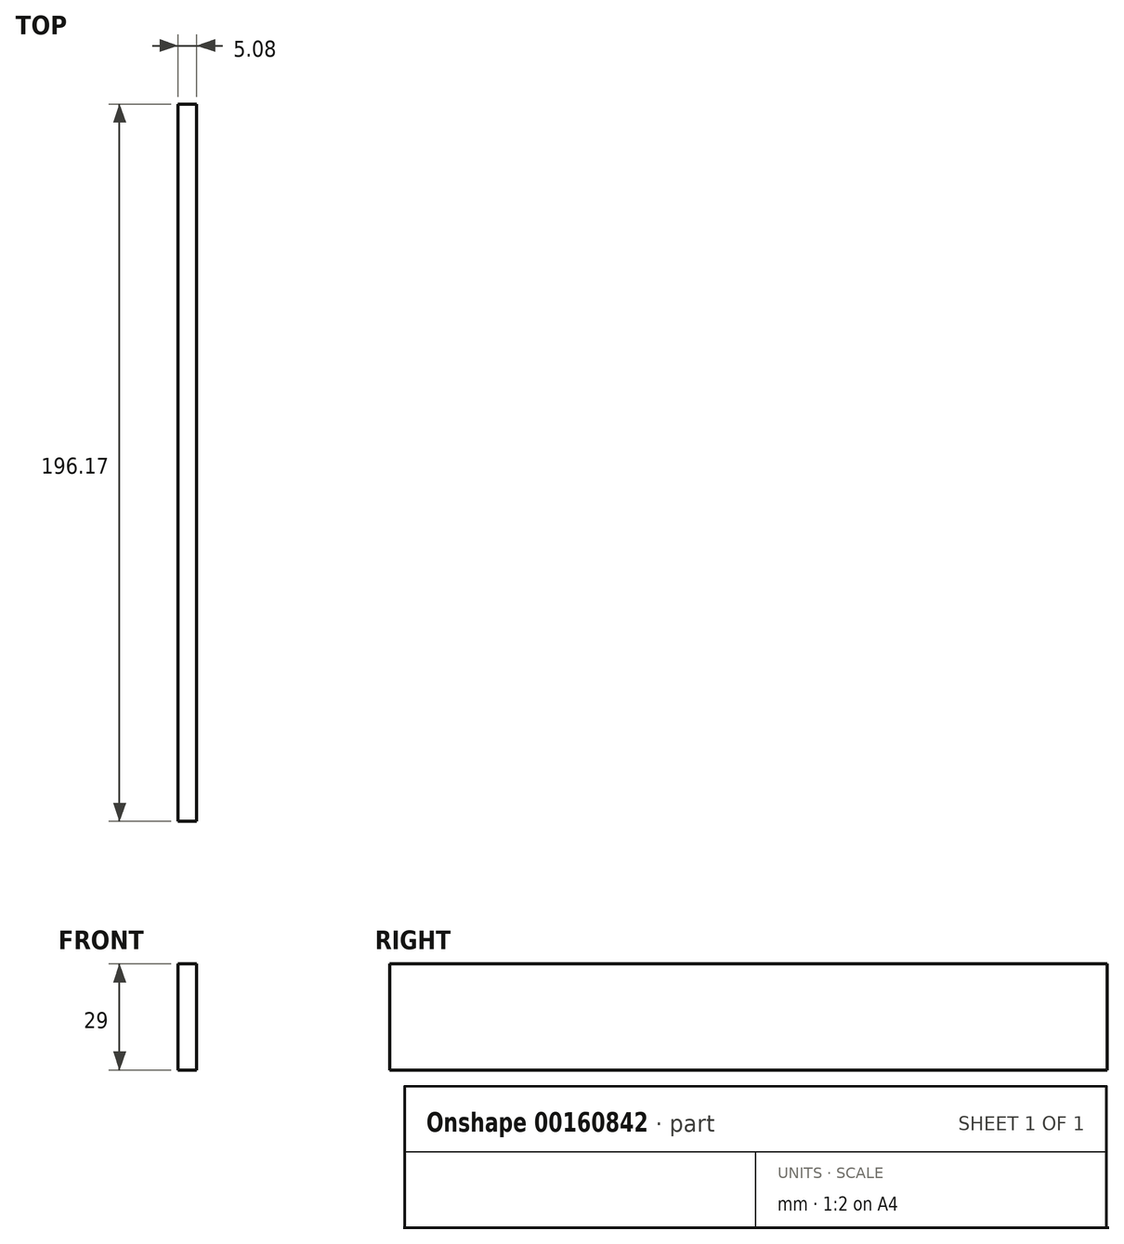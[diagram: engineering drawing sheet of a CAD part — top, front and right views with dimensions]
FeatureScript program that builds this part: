
annotation { "Feature Type Name" : "Feature", "Feature Type Description" : "" }
export const myFeature = defineFeature(function(context is Context, id is Id, definition is map)
    precondition{}
    {
        {
            var Q0;
            Q0=qCreatedBy(makeId("Right.planeOp"),FACE);
            var sketch = newSketch(context, id + "F0", { "sketchPlane" : qUnion([Q0])});
            skLineSegment(sketch, "E0.bottom", {"start": v(-99.71, 58.55) * mm, "end": v(96.46, 58.55) * mm});
            skLineSegment(sketch, "E0.top", {"start": v(-99.71, 29.55) * mm, "end": v(96.46, 29.55) * mm});
            skLineSegment(sketch, "E0.left", {"start": v(-99.71, 58.55) * mm, "end": v(-99.71, 29.55) * mm});
            skLineSegment(sketch, "E0.right", {"start": v(96.46, 58.55) * mm, "end": v(96.46, 29.55) * mm});
            skSolve(sketch);
        }
        {
            var Q0;
            Q0 = qSketchRegion(id + "F0", true);
            extrude(context, id + "F1", {"entities" : qUnion([Q0]), "depth" : 5.08 * mm});
        }
    });
